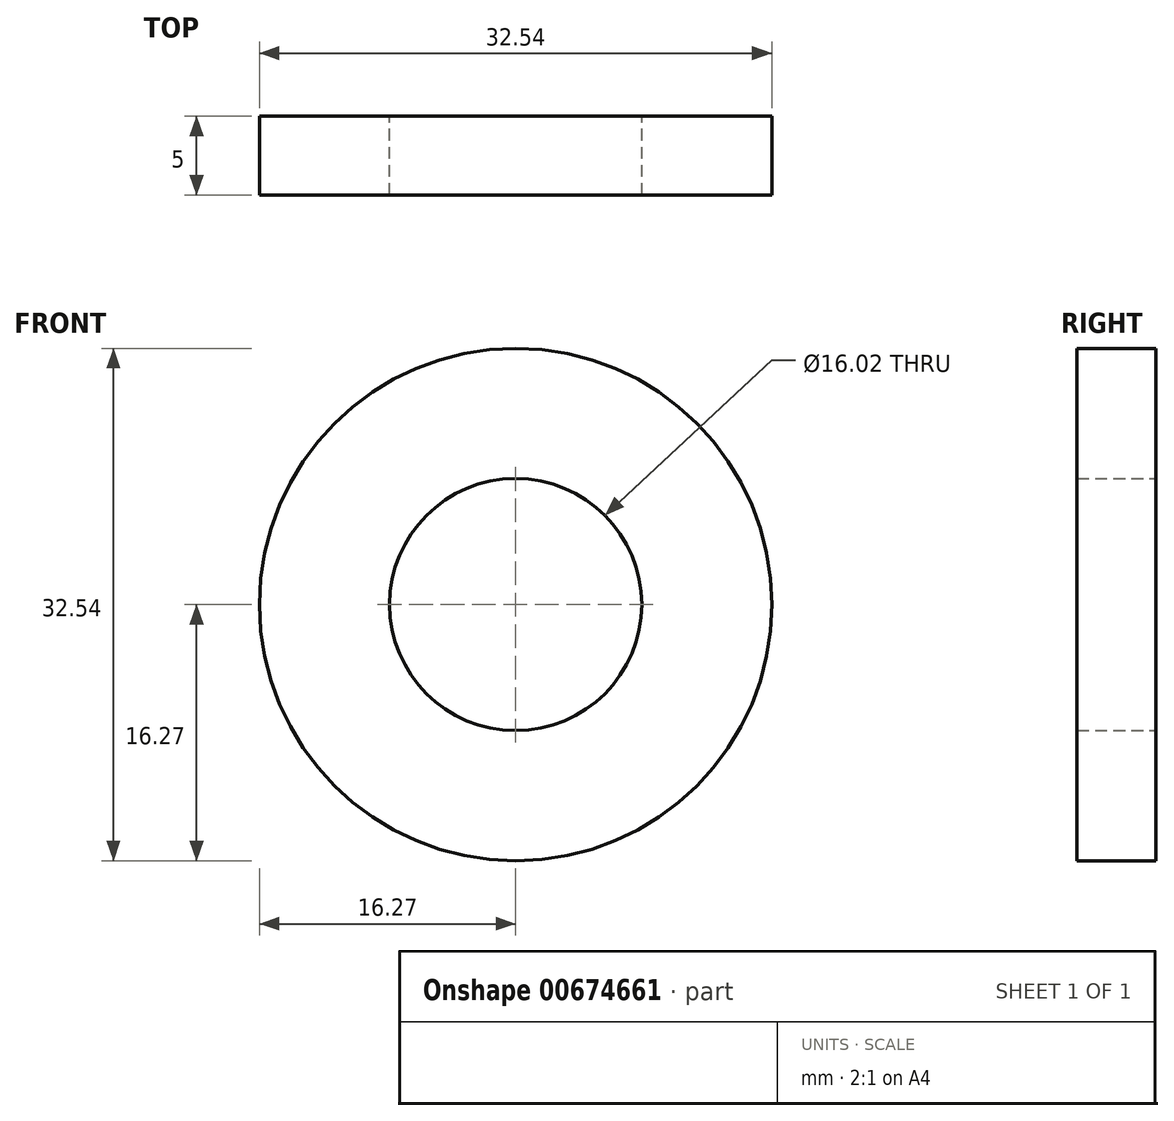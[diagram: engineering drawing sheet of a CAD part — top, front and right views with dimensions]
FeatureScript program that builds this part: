
annotation { "Feature Type Name" : "Feature", "Feature Type Description" : "" }
export const myFeature = defineFeature(function(context is Context, id is Id, definition is map)
    precondition{}
    {
        {
            var Q0;
            Q0=qCreatedBy(makeId("Front.planeOp"),FACE);
            var sketch = newSketch(context, id + "F0", { "sketchPlane" : qUnion([Q0])});
            skCircle(sketch, "E0", {"center": v(0, 0) * mm, "radius": 16.27 * mm});
            skCircle(sketch, "E1", {"center": v(0, 0) * mm, "radius": 8 * mm});
            skSolve(sketch);
        }
        {
            var Q0;
            Q0=makeQuery(id+"F0.imprint","IMPRINT",FACE,{"disambiguationData":[TD([[makeQuery(id+"F0.imprint","IMPRINT",EDGE,{"derivedFrom":sQuery(id+"F0.wireOp",EDGE,"E0")}),1.0]])]});
            extrude(context, id + "F1", {"entities" : qUnion([Q0]), "depth" : 5 * mm, "offsetDistance" : 25 * mm});
        }
    });
